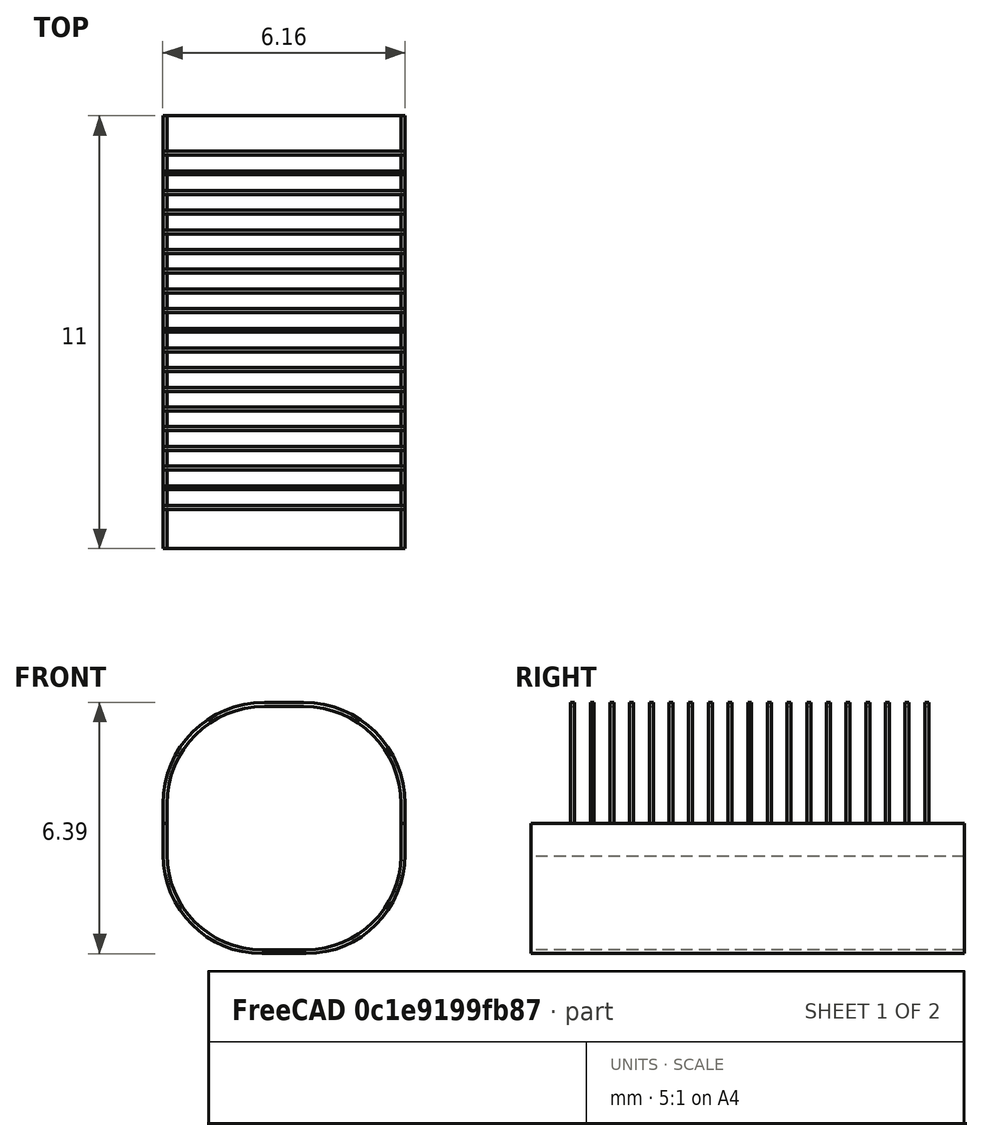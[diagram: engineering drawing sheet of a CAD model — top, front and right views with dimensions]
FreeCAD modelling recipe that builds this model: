
FCSTD DOCUMENT  (FreeCAD 0.16R6712 (Git))
Label: anode
License: All rights reserved
LicenseURL: http://en.wikipedia.org/wiki/All_rights_reserved
objects: Sketcher::SketchObject×39, Part::Sweep×19, Part::MultiFuse×1, PartDesign::Pad×1, Mesh::Feature×1
note: 61 computed .brp shape members not serialized (recipe doc carries the construction recipe); baked Part::Feature solids carry a one-line shape summary decoded from their .brp

FEATURE [Sketcher::SketchObject] Sketch
  Placement = pos=(0,0,0) rot=(1,0,0;1.5708rad)
  sketch-geometry (5):
    g0: LineSegment StartX=-0.5 StartY=3 StartZ=0 EndX=0.5 EndY=3 EndZ=0
    g1: LineSegment StartX=3 StartY=0.5 StartZ=0 EndX=3 EndY=0 EndZ=0
    g2: LineSegment StartX=-3 StartY=0 StartZ=0 EndX=-3 EndY=0.5 EndZ=0
    g3: ArcOfCircle CenterX=-0.5 CenterY=0.5 CenterZ=0 NormalX=0 NormalY=0 NormalZ=1 Radius=2.5 StartAngle=1.5708 EndAngle=3.14159
    g4: ArcOfCircle CenterX=0.5 CenterY=0.5 CenterZ=0 NormalX=0 NormalY=0 NormalZ=1 Radius=2.5 StartAngle=0 EndAngle=1.5708
  constraints (12):
    c: Horizontal(g0)
    c: Vertical(g1)
    c: Tangent(g0,g3) = 1.5708
    c: Tangent(g2,g3) = 1.5708
    c: Tangent(g1,g4) = 1.5708
    c: Tangent(g0,g4) = 1.5708
    c: Equal(g4,g3)
    c: Radius(g4) = 2.5
    c: DistanceY(g-1,g0) = 3
    c: Symmetric(g1,g2,g-2)
    c: DistanceX(g2,g-1) = 3
    c: PointOnObject(g1,g-1)
FEATURE [Sketcher::SketchObject] Sketch001
  sketch-geometry (4):
    g0: LineSegment StartX=2.975 StartY=-0.05 StartZ=0 EndX=3.075 EndY=-0.05 EndZ=0
    g1: LineSegment StartX=3.075 StartY=-0.05 StartZ=0 EndX=3.075 EndY=0.05 EndZ=0
    g2: LineSegment StartX=3.075 StartY=0.05 StartZ=0 EndX=2.975 EndY=0.05 EndZ=0
    g3: LineSegment StartX=2.975 StartY=0.05 StartZ=0 EndX=2.975 EndY=-0.05 EndZ=0
  constraints (12):
    c: Coincident(g0,g1)
    c: Coincident(g1,g2)
    c: Coincident(g2,g3)
    c: Coincident(g3,g0)
    c: Horizontal(g0)
    c: Horizontal(g2)
    c: Vertical(g1)
    c: Vertical(g3)
    c: Distance(g1,g3) = 0.1
    c: DistanceX(g-2,g0) = 2.975
    c: Symmetric(g0,g1,g-1)
    c: DistanceY(g0,g1) = 0.1
FEATURE [Part::Sweep] Sweep
  Frenet = false
  Sections = -> [Sketch001]
  Solid = true
  Spine = -> Sketch [Edge4,Edge3,Edge2,Edge1,Edge5]
  Transition = 1
FEATURE [Sketcher::SketchObject] Sketch002
  Placement = pos=(0,0,0) rot=(1,0,0;1.5708rad)
  sketch-geometry (5):
    g0: LineSegment StartX=-0.5 StartY=3 StartZ=0 EndX=0.5 EndY=3 EndZ=0
    g1: LineSegment StartX=3 StartY=0.5 StartZ=0 EndX=3 EndY=0 EndZ=0
    g2: LineSegment StartX=-3 StartY=0 StartZ=0 EndX=-3 EndY=0.5 EndZ=0
    g3: ArcOfCircle CenterX=-0.5 CenterY=0.5 CenterZ=0 NormalX=0 NormalY=0 NormalZ=1 Radius=2.5 StartAngle=1.5708 EndAngle=3.14159
    g4: ArcOfCircle CenterX=0.5 CenterY=0.5 CenterZ=0 NormalX=0 NormalY=0 NormalZ=1 Radius=2.5 StartAngle=0 EndAngle=1.5708
  constraints (12):
    c: Horizontal(g0)
    c: Vertical(g1)
    c: Tangent(g0,g3) = 1.5708
    c: Tangent(g2,g3) = 1.5708
    c: Tangent(g1,g4) = 1.5708
    c: Tangent(g0,g4) = 1.5708
    c: Equal(g4,g3)
    c: Radius(g4) = 2.5
    c: DistanceY(g-1,g0) = 3
    c: Symmetric(g1,g2,g-2)
    c: DistanceX(g2,g-1) = 3
    c: PointOnObject(g1,g-1)
FEATURE [Sketcher::SketchObject] Sketch003
  sketch-geometry (4):
    g0: LineSegment StartX=2.975 StartY=-0.05 StartZ=0 EndX=3.075 EndY=-0.05 EndZ=0
    g1: LineSegment StartX=3.075 StartY=-0.05 StartZ=0 EndX=3.075 EndY=0.05 EndZ=0
    g2: LineSegment StartX=3.075 StartY=0.05 StartZ=0 EndX=2.975 EndY=0.05 EndZ=0
    g3: LineSegment StartX=2.975 StartY=0.05 StartZ=0 EndX=2.975 EndY=-0.05 EndZ=0
  constraints (12):
    c: Coincident(g0,g1)
    c: Coincident(g1,g2)
    c: Coincident(g2,g3)
    c: Coincident(g3,g0)
    c: Horizontal(g0)
    c: Horizontal(g2)
    c: Vertical(g1)
    c: Vertical(g3)
    c: Distance(g1,g3) = 0.1
    c: DistanceX(g-2,g0) = 2.975
    c: Symmetric(g0,g1,g-1)
    c: DistanceY(g0,g1) = 0.1
FEATURE [Part::Sweep] Sweep001
  Frenet = false
  Placement = pos=(0,0.5,0) rot=(0,0,1;0rad)
  Sections = -> [Sketch003]
  Solid = true
  Spine = -> Sketch002 [Edge4,Edge3,Edge2,Edge1,Edge5]
  Transition = 1
FEATURE [Sketcher::SketchObject] Sketch004
  Placement = pos=(0,0,0) rot=(1,0,0;1.5708rad)
  sketch-geometry (5):
    g0: LineSegment StartX=-0.5 StartY=3 StartZ=0 EndX=0.5 EndY=3 EndZ=0
    g1: LineSegment StartX=3 StartY=0.5 StartZ=0 EndX=3 EndY=0 EndZ=0
    g2: LineSegment StartX=-3 StartY=0 StartZ=0 EndX=-3 EndY=0.5 EndZ=0
    g3: ArcOfCircle CenterX=-0.5 CenterY=0.5 CenterZ=0 NormalX=0 NormalY=0 NormalZ=1 Radius=2.5 StartAngle=1.5708 EndAngle=3.14159
    g4: ArcOfCircle CenterX=0.5 CenterY=0.5 CenterZ=0 NormalX=0 NormalY=0 NormalZ=1 Radius=2.5 StartAngle=0 EndAngle=1.5708
  constraints (12):
    c: Horizontal(g0)
    c: Vertical(g1)
    c: Tangent(g0,g3) = 1.5708
    c: Tangent(g2,g3) = 1.5708
    c: Tangent(g1,g4) = 1.5708
    c: Tangent(g0,g4) = 1.5708
    c: Equal(g4,g3)
    c: Radius(g4) = 2.5
    c: DistanceY(g-1,g0) = 3
    c: Symmetric(g1,g2,g-2)
    c: DistanceX(g2,g-1) = 3
    c: PointOnObject(g1,g-1)
FEATURE [Sketcher::SketchObject] Sketch005
  sketch-geometry (4):
    g0: LineSegment StartX=2.975 StartY=-0.05 StartZ=0 EndX=3.075 EndY=-0.05 EndZ=0
    g1: LineSegment StartX=3.075 StartY=-0.05 StartZ=0 EndX=3.075 EndY=0.05 EndZ=0
    g2: LineSegment StartX=3.075 StartY=0.05 StartZ=0 EndX=2.975 EndY=0.05 EndZ=0
    g3: LineSegment StartX=2.975 StartY=0.05 StartZ=0 EndX=2.975 EndY=-0.05 EndZ=0
  constraints (12):
    c: Coincident(g0,g1)
    c: Coincident(g1,g2)
    c: Coincident(g2,g3)
    c: Coincident(g3,g0)
    c: Horizontal(g0)
    c: Horizontal(g2)
    c: Vertical(g1)
    c: Vertical(g3)
    c: Distance(g1,g3) = 0.1
    c: DistanceX(g-2,g0) = 2.975
    c: Symmetric(g0,g1,g-1)
    c: DistanceY(g0,g1) = 0.1
FEATURE [Part::Sweep] Sweep002
  Frenet = false
  Placement = pos=(0,1,0) rot=(0,0,1;0rad)
  Sections = -> [Sketch005]
  Solid = true
  Spine = -> Sketch004 [Edge4,Edge3,Edge2,Edge1,Edge5]
  Transition = 1
FEATURE [Sketcher::SketchObject] Sketch006
  Placement = pos=(0,0,0) rot=(1,0,0;1.5708rad)
  sketch-geometry (5):
    g0: LineSegment StartX=-0.5 StartY=3 StartZ=0 EndX=0.5 EndY=3 EndZ=0
    g1: LineSegment StartX=3 StartY=0.5 StartZ=0 EndX=3 EndY=0 EndZ=0
    g2: LineSegment StartX=-3 StartY=0 StartZ=0 EndX=-3 EndY=0.5 EndZ=0
    g3: ArcOfCircle CenterX=-0.5 CenterY=0.5 CenterZ=0 NormalX=0 NormalY=0 NormalZ=1 Radius=2.5 StartAngle=1.5708 EndAngle=3.14159
    g4: ArcOfCircle CenterX=0.5 CenterY=0.5 CenterZ=0 NormalX=0 NormalY=0 NormalZ=1 Radius=2.5 StartAngle=0 EndAngle=1.5708
  constraints (12):
    c: Horizontal(g0)
    c: Vertical(g1)
    c: Tangent(g0,g3) = 1.5708
    c: Tangent(g2,g3) = 1.5708
    c: Tangent(g1,g4) = 1.5708
    c: Tangent(g0,g4) = 1.5708
    c: Equal(g4,g3)
    c: Radius(g4) = 2.5
    c: DistanceY(g-1,g0) = 3
    c: Symmetric(g1,g2,g-2)
    c: DistanceX(g2,g-1) = 3
    c: PointOnObject(g1,g-1)
FEATURE [Sketcher::SketchObject] Sketch007
  sketch-geometry (4):
    g0: LineSegment StartX=2.975 StartY=-0.05 StartZ=0 EndX=3.075 EndY=-0.05 EndZ=0
    g1: LineSegment StartX=3.075 StartY=-0.05 StartZ=0 EndX=3.075 EndY=0.05 EndZ=0
    g2: LineSegment StartX=3.075 StartY=0.05 StartZ=0 EndX=2.975 EndY=0.05 EndZ=0
    g3: LineSegment StartX=2.975 StartY=0.05 StartZ=0 EndX=2.975 EndY=-0.05 EndZ=0
  constraints (12):
    c: Coincident(g0,g1)
    c: Coincident(g1,g2)
    c: Coincident(g2,g3)
    c: Coincident(g3,g0)
    c: Horizontal(g0)
    c: Horizontal(g2)
    c: Vertical(g1)
    c: Vertical(g3)
    c: Distance(g1,g3) = 0.1
    c: DistanceX(g-2,g0) = 2.975
    c: Symmetric(g0,g1,g-1)
    c: DistanceY(g0,g1) = 0.1
FEATURE [Part::Sweep] Sweep003
  Frenet = false
  Placement = pos=(0,1.5,0) rot=(0,0,1;0rad)
  Sections = -> [Sketch007]
  Solid = true
  Spine = -> Sketch006 [Edge4,Edge3,Edge2,Edge1,Edge5]
  Transition = 1
FEATURE [Sketcher::SketchObject] Sketch008
  Placement = pos=(0,2,0) rot=(1,0,0;1.5708rad)
  sketch-geometry (5):
    g0: LineSegment StartX=-0.5 StartY=3 StartZ=0 EndX=0.5 EndY=3 EndZ=0
    g1: LineSegment StartX=3 StartY=0.5 StartZ=0 EndX=3 EndY=0 EndZ=0
    g2: LineSegment StartX=-3 StartY=0 StartZ=0 EndX=-3 EndY=0.5 EndZ=0
    g3: ArcOfCircle CenterX=-0.5 CenterY=0.5 CenterZ=0 NormalX=0 NormalY=0 NormalZ=1 Radius=2.5 StartAngle=1.5708 EndAngle=3.14159
    g4: ArcOfCircle CenterX=0.5 CenterY=0.5 CenterZ=0 NormalX=0 NormalY=0 NormalZ=1 Radius=2.5 StartAngle=0 EndAngle=1.5708
  constraints (12):
    c: Horizontal(g0)
    c: Vertical(g1)
    c: Tangent(g0,g3) = 1.5708
    c: Tangent(g2,g3) = 1.5708
    c: Tangent(g1,g4) = 1.5708
    c: Tangent(g0,g4) = 1.5708
    c: Equal(g4,g3)
    c: Radius(g4) = 2.5
    c: DistanceY(g-1,g0) = 3
    c: Symmetric(g1,g2,g-2)
    c: DistanceX(g2,g-1) = 3
    c: PointOnObject(g1,g-1)
FEATURE [Sketcher::SketchObject] Sketch009
  sketch-geometry (4):
    g0: LineSegment StartX=2.975 StartY=-0.05 StartZ=0 EndX=3.075 EndY=-0.05 EndZ=0
    g1: LineSegment StartX=3.075 StartY=-0.05 StartZ=0 EndX=3.075 EndY=0.05 EndZ=0
    g2: LineSegment StartX=3.075 StartY=0.05 StartZ=0 EndX=2.975 EndY=0.05 EndZ=0
    g3: LineSegment StartX=2.975 StartY=0.05 StartZ=0 EndX=2.975 EndY=-0.05 EndZ=0
  constraints (12):
    c: Coincident(g0,g1)
    c: Coincident(g1,g2)
    c: Coincident(g2,g3)
    c: Coincident(g3,g0)
    c: Horizontal(g0)
    c: Horizontal(g2)
    c: Vertical(g1)
    c: Vertical(g3)
    c: Distance(g1,g3) = 0.1
    c: DistanceX(g-2,g0) = 2.975
    c: Symmetric(g0,g1,g-1)
    c: DistanceY(g0,g1) = 0.1
FEATURE [Part::Sweep] Sweep004
  Frenet = false
  Placement = pos=(0,2,0) rot=(0,0,1;0rad)
  Sections = -> [Sketch009]
  Solid = true
  Spine = -> Sketch008 [Edge4,Edge3,Edge2,Edge1,Edge5]
  Transition = 1
FEATURE [Sketcher::SketchObject] Sketch010
  Placement = pos=(0,0,0) rot=(1,0,0;1.5708rad)
  sketch-geometry (5):
    g0: LineSegment StartX=-0.5 StartY=3 StartZ=0 EndX=0.5 EndY=3 EndZ=0
    g1: LineSegment StartX=3 StartY=0.5 StartZ=0 EndX=3 EndY=0 EndZ=0
    g2: LineSegment StartX=-3 StartY=0 StartZ=0 EndX=-3 EndY=0.5 EndZ=0
    g3: ArcOfCircle CenterX=-0.5 CenterY=0.5 CenterZ=0 NormalX=0 NormalY=0 NormalZ=1 Radius=2.5 StartAngle=1.5708 EndAngle=3.14159
    g4: ArcOfCircle CenterX=0.5 CenterY=0.5 CenterZ=0 NormalX=0 NormalY=0 NormalZ=1 Radius=2.5 StartAngle=0 EndAngle=1.5708
  constraints (12):
    c: Horizontal(g0)
    c: Vertical(g1)
    c: Tangent(g0,g3) = 1.5708
    c: Tangent(g2,g3) = 1.5708
    c: Tangent(g1,g4) = 1.5708
    c: Tangent(g0,g4) = 1.5708
    c: Equal(g4,g3)
    c: Radius(g4) = 2.5
    c: DistanceY(g-1,g0) = 3
    c: Symmetric(g1,g2,g-2)
    c: DistanceX(g2,g-1) = 3
    c: PointOnObject(g1,g-1)
FEATURE [Sketcher::SketchObject] Sketch011
  sketch-geometry (4):
    g0: LineSegment StartX=2.975 StartY=-0.05 StartZ=0 EndX=3.075 EndY=-0.05 EndZ=0
    g1: LineSegment StartX=3.075 StartY=-0.05 StartZ=0 EndX=3.075 EndY=0.05 EndZ=0
    g2: LineSegment StartX=3.075 StartY=0.05 StartZ=0 EndX=2.975 EndY=0.05 EndZ=0
    g3: LineSegment StartX=2.975 StartY=0.05 StartZ=0 EndX=2.975 EndY=-0.05 EndZ=0
  constraints (12):
    c: Coincident(g0,g1)
    c: Coincident(g1,g2)
    c: Coincident(g2,g3)
    c: Coincident(g3,g0)
    c: Horizontal(g0)
    c: Horizontal(g2)
    c: Vertical(g1)
    c: Vertical(g3)
    c: Distance(g1,g3) = 0.1
    c: DistanceX(g-2,g0) = 2.975
    c: Symmetric(g0,g1,g-1)
    c: DistanceY(g0,g1) = 0.1
FEATURE [Part::Sweep] Sweep005
  Frenet = false
  Placement = pos=(0,2.5,0) rot=(0,0,1;0rad)
  Sections = -> [Sketch011]
  Solid = true
  Spine = -> Sketch010 [Edge4,Edge3,Edge2,Edge1,Edge5]
  Transition = 1
FEATURE [Sketcher::SketchObject] Sketch012
  Placement = pos=(0,0,0) rot=(1,0,0;1.5708rad)
  sketch-geometry (5):
    g0: LineSegment StartX=-0.5 StartY=3 StartZ=0 EndX=0.5 EndY=3 EndZ=0
    g1: LineSegment StartX=3 StartY=0.5 StartZ=0 EndX=3 EndY=0 EndZ=0
    g2: LineSegment StartX=-3 StartY=0 StartZ=0 EndX=-3 EndY=0.5 EndZ=0
    g3: ArcOfCircle CenterX=-0.5 CenterY=0.5 CenterZ=0 NormalX=0 NormalY=0 NormalZ=1 Radius=2.5 StartAngle=1.5708 EndAngle=3.14159
    g4: ArcOfCircle CenterX=0.5 CenterY=0.5 CenterZ=0 NormalX=0 NormalY=0 NormalZ=1 Radius=2.5 StartAngle=0 EndAngle=1.5708
  constraints (12):
    c: Horizontal(g0)
    c: Vertical(g1)
    c: Tangent(g0,g3) = 1.5708
    c: Tangent(g2,g3) = 1.5708
    c: Tangent(g1,g4) = 1.5708
    c: Tangent(g0,g4) = 1.5708
    c: Equal(g4,g3)
    c: Radius(g4) = 2.5
    c: DistanceY(g-1,g0) = 3
    c: Symmetric(g1,g2,g-2)
    c: DistanceX(g2,g-1) = 3
    c: PointOnObject(g1,g-1)
FEATURE [Sketcher::SketchObject] Sketch013
  sketch-geometry (4):
    g0: LineSegment StartX=2.975 StartY=-0.05 StartZ=0 EndX=3.075 EndY=-0.05 EndZ=0
    g1: LineSegment StartX=3.075 StartY=-0.05 StartZ=0 EndX=3.075 EndY=0.05 EndZ=0
    g2: LineSegment StartX=3.075 StartY=0.05 StartZ=0 EndX=2.975 EndY=0.05 EndZ=0
    g3: LineSegment StartX=2.975 StartY=0.05 StartZ=0 EndX=2.975 EndY=-0.05 EndZ=0
  constraints (12):
    c: Coincident(g0,g1)
    c: Coincident(g1,g2)
    c: Coincident(g2,g3)
    c: Coincident(g3,g0)
    c: Horizontal(g0)
    c: Horizontal(g2)
    c: Vertical(g1)
    c: Vertical(g3)
    c: Distance(g1,g3) = 0.1
    c: DistanceX(g-2,g0) = 2.975
    c: Symmetric(g0,g1,g-1)
    c: DistanceY(g0,g1) = 0.1
FEATURE [Part::Sweep] Sweep006
  Frenet = false
  Placement = pos=(0,3,0) rot=(0,0,1;0rad)
  Sections = -> [Sketch013]
  Solid = true
  Spine = -> Sketch012 [Edge4,Edge3,Edge2,Edge1,Edge5]
  Transition = 1
FEATURE [Sketcher::SketchObject] Sketch014
  Placement = pos=(0,0,0) rot=(1,0,0;1.5708rad)
  sketch-geometry (5):
    g0: LineSegment StartX=-0.5 StartY=3 StartZ=0 EndX=0.5 EndY=3 EndZ=0
    g1: LineSegment StartX=3 StartY=0.5 StartZ=0 EndX=3 EndY=0 EndZ=0
    g2: LineSegment StartX=-3 StartY=0 StartZ=0 EndX=-3 EndY=0.5 EndZ=0
    g3: ArcOfCircle CenterX=-0.5 CenterY=0.5 CenterZ=0 NormalX=0 NormalY=0 NormalZ=1 Radius=2.5 StartAngle=1.5708 EndAngle=3.14159
    g4: ArcOfCircle CenterX=0.5 CenterY=0.5 CenterZ=0 NormalX=0 NormalY=0 NormalZ=1 Radius=2.5 StartAngle=0 EndAngle=1.5708
  constraints (12):
    c: Horizontal(g0)
    c: Vertical(g1)
    c: Tangent(g0,g3) = 1.5708
    c: Tangent(g2,g3) = 1.5708
    c: Tangent(g1,g4) = 1.5708
    c: Tangent(g0,g4) = 1.5708
    c: Equal(g4,g3)
    c: Radius(g4) = 2.5
    c: DistanceY(g-1,g0) = 3
    c: Symmetric(g1,g2,g-2)
    c: DistanceX(g2,g-1) = 3
    c: PointOnObject(g1,g-1)
FEATURE [Sketcher::SketchObject] Sketch015
  sketch-geometry (4):
    g0: LineSegment StartX=2.975 StartY=-0.05 StartZ=0 EndX=3.075 EndY=-0.05 EndZ=0
    g1: LineSegment StartX=3.075 StartY=-0.05 StartZ=0 EndX=3.075 EndY=0.05 EndZ=0
    g2: LineSegment StartX=3.075 StartY=0.05 StartZ=0 EndX=2.975 EndY=0.05 EndZ=0
    g3: LineSegment StartX=2.975 StartY=0.05 StartZ=0 EndX=2.975 EndY=-0.05 EndZ=0
  constraints (12):
    c: Coincident(g0,g1)
    c: Coincident(g1,g2)
    c: Coincident(g2,g3)
    c: Coincident(g3,g0)
    c: Horizontal(g0)
    c: Horizontal(g2)
    c: Vertical(g1)
    c: Vertical(g3)
    c: Distance(g1,g3) = 0.1
    c: DistanceX(g-2,g0) = 2.975
    c: Symmetric(g0,g1,g-1)
    c: DistanceY(g0,g1) = 0.1
FEATURE [Part::Sweep] Sweep007
  Frenet = false
  Placement = pos=(0,3.5,0) rot=(0,0,1;0rad)
  Sections = -> [Sketch015]
  Solid = true
  Spine = -> Sketch014 [Edge4,Edge3,Edge2,Edge1,Edge5]
  Transition = 1
FEATURE [Sketcher::SketchObject] Sketch016
  Placement = pos=(0,0,0) rot=(1,0,0;1.5708rad)
  sketch-geometry (5):
    g0: LineSegment StartX=-0.5 StartY=3 StartZ=0 EndX=0.5 EndY=3 EndZ=0
    g1: LineSegment StartX=3 StartY=0.5 StartZ=0 EndX=3 EndY=0 EndZ=0
    g2: LineSegment StartX=-3 StartY=0 StartZ=0 EndX=-3 EndY=0.5 EndZ=0
    g3: ArcOfCircle CenterX=-0.5 CenterY=0.5 CenterZ=0 NormalX=0 NormalY=0 NormalZ=1 Radius=2.5 StartAngle=1.5708 EndAngle=3.14159
    g4: ArcOfCircle CenterX=0.5 CenterY=0.5 CenterZ=0 NormalX=0 NormalY=0 NormalZ=1 Radius=2.5 StartAngle=0 EndAngle=1.5708
  constraints (12):
    c: Horizontal(g0)
    c: Vertical(g1)
    c: Tangent(g0,g3) = 1.5708
    c: Tangent(g2,g3) = 1.5708
    c: Tangent(g1,g4) = 1.5708
    c: Tangent(g0,g4) = 1.5708
    c: Equal(g4,g3)
    c: Radius(g4) = 2.5
    c: DistanceY(g-1,g0) = 3
    c: Symmetric(g1,g2,g-2)
    c: DistanceX(g2,g-1) = 3
    c: PointOnObject(g1,g-1)
FEATURE [Sketcher::SketchObject] Sketch017
  sketch-geometry (4):
    g0: LineSegment StartX=2.975 StartY=-0.05 StartZ=0 EndX=3.075 EndY=-0.05 EndZ=0
    g1: LineSegment StartX=3.075 StartY=-0.05 StartZ=0 EndX=3.075 EndY=0.05 EndZ=0
    g2: LineSegment StartX=3.075 StartY=0.05 StartZ=0 EndX=2.975 EndY=0.05 EndZ=0
    g3: LineSegment StartX=2.975 StartY=0.05 StartZ=0 EndX=2.975 EndY=-0.05 EndZ=0
  constraints (12):
    c: Coincident(g0,g1)
    c: Coincident(g1,g2)
    c: Coincident(g2,g3)
    c: Coincident(g3,g0)
    c: Horizontal(g0)
    c: Horizontal(g2)
    c: Vertical(g1)
    c: Vertical(g3)
    c: Distance(g1,g3) = 0.1
    c: DistanceX(g-2,g0) = 2.975
    c: Symmetric(g0,g1,g-1)
    c: DistanceY(g0,g1) = 0.1
FEATURE [Part::Sweep] Sweep008
  Frenet = false
  Placement = pos=(0,4,0) rot=(0,0,1;0rad)
  Sections = -> [Sketch017]
  Solid = true
  Spine = -> Sketch016 [Edge4,Edge3,Edge2,Edge1,Edge5]
  Transition = 1
FEATURE [Sketcher::SketchObject] Sketch018
  Placement = pos=(0,0,0) rot=(1,0,0;1.5708rad)
  sketch-geometry (5):
    g0: LineSegment StartX=-0.5 StartY=3 StartZ=0 EndX=0.5 EndY=3 EndZ=0
    g1: LineSegment StartX=3 StartY=0.5 StartZ=0 EndX=3 EndY=0 EndZ=0
    g2: LineSegment StartX=-3 StartY=0 StartZ=0 EndX=-3 EndY=0.5 EndZ=0
    g3: ArcOfCircle CenterX=-0.5 CenterY=0.5 CenterZ=0 NormalX=0 NormalY=0 NormalZ=1 Radius=2.5 StartAngle=1.5708 EndAngle=3.14159
    g4: ArcOfCircle CenterX=0.5 CenterY=0.5 CenterZ=0 NormalX=0 NormalY=0 NormalZ=1 Radius=2.5 StartAngle=0 EndAngle=1.5708
  constraints (12):
    c: Horizontal(g0)
    c: Vertical(g1)
    c: Tangent(g0,g3) = 1.5708
    c: Tangent(g2,g3) = 1.5708
    c: Tangent(g1,g4) = 1.5708
    c: Tangent(g0,g4) = 1.5708
    c: Equal(g4,g3)
    c: Radius(g4) = 2.5
    c: DistanceY(g-1,g0) = 3
    c: Symmetric(g1,g2,g-2)
    c: DistanceX(g2,g-1) = 3
    c: PointOnObject(g1,g-1)
FEATURE [Sketcher::SketchObject] Sketch019
  sketch-geometry (4):
    g0: LineSegment StartX=2.975 StartY=-0.05 StartZ=0 EndX=3.075 EndY=-0.05 EndZ=0
    g1: LineSegment StartX=3.075 StartY=-0.05 StartZ=0 EndX=3.075 EndY=0.05 EndZ=0
    g2: LineSegment StartX=3.075 StartY=0.05 StartZ=0 EndX=2.975 EndY=0.05 EndZ=0
    g3: LineSegment StartX=2.975 StartY=0.05 StartZ=0 EndX=2.975 EndY=-0.05 EndZ=0
  constraints (12):
    c: Coincident(g0,g1)
    c: Coincident(g1,g2)
    c: Coincident(g2,g3)
    c: Coincident(g3,g0)
    c: Horizontal(g0)
    c: Horizontal(g2)
    c: Vertical(g1)
    c: Vertical(g3)
    c: Distance(g1,g3) = 0.1
    c: DistanceX(g-2,g0) = 2.975
    c: Symmetric(g0,g1,g-1)
    c: DistanceY(g0,g1) = 0.1
FEATURE [Part::Sweep] Sweep009
  Frenet = false
  Placement = pos=(0,4.5,0) rot=(0,0,1;0rad)
  Sections = -> [Sketch019]
  Solid = true
  Spine = -> Sketch018 [Edge4,Edge3,Edge2,Edge1,Edge5]
  Transition = 1
FEATURE [Sketcher::SketchObject] Sketch020
  Placement = pos=(0,0,0) rot=(1,0,0;1.5708rad)
  sketch-geometry (5):
    g0: LineSegment StartX=-0.5 StartY=3 StartZ=0 EndX=0.5 EndY=3 EndZ=0
    g1: LineSegment StartX=3 StartY=0.5 StartZ=0 EndX=3 EndY=0 EndZ=0
    g2: LineSegment StartX=-3 StartY=0 StartZ=0 EndX=-3 EndY=0.5 EndZ=0
    g3: ArcOfCircle CenterX=-0.5 CenterY=0.5 CenterZ=0 NormalX=0 NormalY=0 NormalZ=1 Radius=2.5 StartAngle=1.5708 EndAngle=3.14159
    g4: ArcOfCircle CenterX=0.5 CenterY=0.5 CenterZ=0 NormalX=0 NormalY=0 NormalZ=1 Radius=2.5 StartAngle=0 EndAngle=1.5708
  constraints (12):
    c: Horizontal(g0)
    c: Vertical(g1)
    c: Tangent(g0,g3) = 1.5708
    c: Tangent(g2,g3) = 1.5708
    c: Tangent(g1,g4) = 1.5708
    c: Tangent(g0,g4) = 1.5708
    c: Equal(g4,g3)
    c: Radius(g4) = 2.5
    c: DistanceY(g-1,g0) = 3
    c: Symmetric(g1,g2,g-2)
    c: DistanceX(g2,g-1) = 3
    c: PointOnObject(g1,g-1)
FEATURE [Sketcher::SketchObject] Sketch021
  sketch-geometry (4):
    g0: LineSegment StartX=2.975 StartY=-0.05 StartZ=0 EndX=3.075 EndY=-0.05 EndZ=0
    g1: LineSegment StartX=3.075 StartY=-0.05 StartZ=0 EndX=3.075 EndY=0.05 EndZ=0
    g2: LineSegment StartX=3.075 StartY=0.05 StartZ=0 EndX=2.975 EndY=0.05 EndZ=0
    g3: LineSegment StartX=2.975 StartY=0.05 StartZ=0 EndX=2.975 EndY=-0.05 EndZ=0
  constraints (12):
    c: Coincident(g0,g1)
    c: Coincident(g1,g2)
    c: Coincident(g2,g3)
    c: Coincident(g3,g0)
    c: Horizontal(g0)
    c: Horizontal(g2)
    c: Vertical(g1)
    c: Vertical(g3)
    c: Distance(g1,g3) = 0.1
    c: DistanceX(g-2,g0) = 2.975
    c: Symmetric(g0,g1,g-1)
    c: DistanceY(g0,g1) = 0.1
FEATURE [Part::Sweep] Sweep010
  Frenet = false
  Placement = pos=(0,5,0) rot=(0,0,1;0rad)
  Sections = -> [Sketch021]
  Solid = true
  Spine = -> Sketch020 [Edge4,Edge3,Edge2,Edge1,Edge5]
  Transition = 1
FEATURE [Sketcher::SketchObject] Sketch022
  Placement = pos=(0,0,0) rot=(1,0,0;1.5708rad)
  sketch-geometry (5):
    g0: LineSegment StartX=-0.5 StartY=3 StartZ=0 EndX=0.5 EndY=3 EndZ=0
    g1: LineSegment StartX=3 StartY=0.5 StartZ=0 EndX=3 EndY=0 EndZ=0
    g2: LineSegment StartX=-3 StartY=0 StartZ=0 EndX=-3 EndY=0.5 EndZ=0
    g3: ArcOfCircle CenterX=-0.5 CenterY=0.5 CenterZ=0 NormalX=0 NormalY=0 NormalZ=1 Radius=2.5 StartAngle=1.5708 EndAngle=3.14159
    g4: ArcOfCircle CenterX=0.5 CenterY=0.5 CenterZ=0 NormalX=0 NormalY=0 NormalZ=1 Radius=2.5 StartAngle=0 EndAngle=1.5708
  constraints (12):
    c: Horizontal(g0)
    c: Vertical(g1)
    c: Tangent(g0,g3) = 1.5708
    c: Tangent(g2,g3) = 1.5708
    c: Tangent(g1,g4) = 1.5708
    c: Tangent(g0,g4) = 1.5708
    c: Equal(g4,g3)
    c: Radius(g4) = 2.5
    c: DistanceY(g-1,g0) = 3
    c: Symmetric(g1,g2,g-2)
    c: DistanceX(g2,g-1) = 3
    c: PointOnObject(g1,g-1)
FEATURE [Sketcher::SketchObject] Sketch023
  sketch-geometry (4):
    g0: LineSegment StartX=2.975 StartY=-0.05 StartZ=0 EndX=3.075 EndY=-0.05 EndZ=0
    g1: LineSegment StartX=3.075 StartY=-0.05 StartZ=0 EndX=3.075 EndY=0.05 EndZ=0
    g2: LineSegment StartX=3.075 StartY=0.05 StartZ=0 EndX=2.975 EndY=0.05 EndZ=0
    g3: LineSegment StartX=2.975 StartY=0.05 StartZ=0 EndX=2.975 EndY=-0.05 EndZ=0
  constraints (12):
    c: Coincident(g0,g1)
    c: Coincident(g1,g2)
    c: Coincident(g2,g3)
    c: Coincident(g3,g0)
    c: Horizontal(g0)
    c: Horizontal(g2)
    c: Vertical(g1)
    c: Vertical(g3)
    c: Distance(g1,g3) = 0.1
    c: DistanceX(g-2,g0) = 2.975
    c: Symmetric(g0,g1,g-1)
    c: DistanceY(g0,g1) = 0.1
FEATURE [Part::Sweep] Sweep011
  Frenet = false
  Placement = pos=(0,5.5,0) rot=(0,0,1;0rad)
  Sections = -> [Sketch023]
  Solid = true
  Spine = -> Sketch022 [Edge4,Edge3,Edge2,Edge1,Edge5]
  Transition = 1
FEATURE [Sketcher::SketchObject] Sketch024
  Placement = pos=(0,0,0) rot=(1,0,0;1.5708rad)
  sketch-geometry (5):
    g0: LineSegment StartX=-0.5 StartY=3 StartZ=0 EndX=0.5 EndY=3 EndZ=0
    g1: LineSegment StartX=3 StartY=0.5 StartZ=0 EndX=3 EndY=0 EndZ=0
    g2: LineSegment StartX=-3 StartY=0 StartZ=0 EndX=-3 EndY=0.5 EndZ=0
    g3: ArcOfCircle CenterX=-0.5 CenterY=0.5 CenterZ=0 NormalX=0 NormalY=0 NormalZ=1 Radius=2.5 StartAngle=1.5708 EndAngle=3.14159
    g4: ArcOfCircle CenterX=0.5 CenterY=0.5 CenterZ=0 NormalX=0 NormalY=0 NormalZ=1 Radius=2.5 StartAngle=0 EndAngle=1.5708
  constraints (12):
    c: Horizontal(g0)
    c: Vertical(g1)
    c: Tangent(g0,g3) = 1.5708
    c: Tangent(g2,g3) = 1.5708
    c: Tangent(g1,g4) = 1.5708
    c: Tangent(g0,g4) = 1.5708
    c: Equal(g4,g3)
    c: Radius(g4) = 2.5
    c: DistanceY(g-1,g0) = 3
    c: Symmetric(g1,g2,g-2)
    c: DistanceX(g2,g-1) = 3
    c: PointOnObject(g1,g-1)
FEATURE [Sketcher::SketchObject] Sketch025
  sketch-geometry (4):
    g0: LineSegment StartX=2.975 StartY=-0.05 StartZ=0 EndX=3.075 EndY=-0.05 EndZ=0
    g1: LineSegment StartX=3.075 StartY=-0.05 StartZ=0 EndX=3.075 EndY=0.05 EndZ=0
    g2: LineSegment StartX=3.075 StartY=0.05 StartZ=0 EndX=2.975 EndY=0.05 EndZ=0
    g3: LineSegment StartX=2.975 StartY=0.05 StartZ=0 EndX=2.975 EndY=-0.05 EndZ=0
  constraints (12):
    c: Coincident(g0,g1)
    c: Coincident(g1,g2)
    c: Coincident(g2,g3)
    c: Coincident(g3,g0)
    c: Horizontal(g0)
    c: Horizontal(g2)
    c: Vertical(g1)
    c: Vertical(g3)
    c: Distance(g1,g3) = 0.1
    c: DistanceX(g-2,g0) = 2.975
    c: Symmetric(g0,g1,g-1)
    c: DistanceY(g0,g1) = 0.1
FEATURE [Part::Sweep] Sweep012
  Frenet = false
  Placement = pos=(0,6,0) rot=(0,0,1;0rad)
  Sections = -> [Sketch025]
  Solid = true
  Spine = -> Sketch024 [Edge4,Edge3,Edge2,Edge1,Edge5]
  Transition = 1
FEATURE [Sketcher::SketchObject] Sketch026
  Placement = pos=(0,0,0) rot=(1,0,0;1.5708rad)
  sketch-geometry (5):
    g0: LineSegment StartX=-0.5 StartY=3 StartZ=0 EndX=0.5 EndY=3 EndZ=0
    g1: LineSegment StartX=3 StartY=0.5 StartZ=0 EndX=3 EndY=0 EndZ=0
    g2: LineSegment StartX=-3 StartY=0 StartZ=0 EndX=-3 EndY=0.5 EndZ=0
    g3: ArcOfCircle CenterX=-0.5 CenterY=0.5 CenterZ=0 NormalX=0 NormalY=0 NormalZ=1 Radius=2.5 StartAngle=1.5708 EndAngle=3.14159
    g4: ArcOfCircle CenterX=0.5 CenterY=0.5 CenterZ=0 NormalX=0 NormalY=0 NormalZ=1 Radius=2.5 StartAngle=0 EndAngle=1.5708
  constraints (12):
    c: Horizontal(g0)
    c: Vertical(g1)
    c: Tangent(g0,g3) = 1.5708
    c: Tangent(g2,g3) = 1.5708
    c: Tangent(g1,g4) = 1.5708
    c: Tangent(g0,g4) = 1.5708
    c: Equal(g4,g3)
    c: Radius(g4) = 2.5
    c: DistanceY(g-1,g0) = 3
    c: Symmetric(g1,g2,g-2)
    c: DistanceX(g2,g-1) = 3
    c: PointOnObject(g1,g-1)
FEATURE [Sketcher::SketchObject] Sketch027
  sketch-geometry (4):
    g0: LineSegment StartX=2.975 StartY=-0.05 StartZ=0 EndX=3.075 EndY=-0.05 EndZ=0
    g1: LineSegment StartX=3.075 StartY=-0.05 StartZ=0 EndX=3.075 EndY=0.05 EndZ=0
    g2: LineSegment StartX=3.075 StartY=0.05 StartZ=0 EndX=2.975 EndY=0.05 EndZ=0
    g3: LineSegment StartX=2.975 StartY=0.05 StartZ=0 EndX=2.975 EndY=-0.05 EndZ=0
  constraints (12):
    c: Coincident(g0,g1)
    c: Coincident(g1,g2)
    c: Coincident(g2,g3)
    c: Coincident(g3,g0)
    c: Horizontal(g0)
    c: Horizontal(g2)
    c: Vertical(g1)
    c: Vertical(g3)
    c: Distance(g1,g3) = 0.1
    c: DistanceX(g-2,g0) = 2.975
    c: Symmetric(g0,g1,g-1)
    c: DistanceY(g0,g1) = 0.1
FEATURE [Part::Sweep] Sweep013
  Frenet = false
  Placement = pos=(0,6.5,0) rot=(0,0,1;0rad)
  Sections = -> [Sketch027]
  Solid = true
  Spine = -> Sketch026 [Edge4,Edge3,Edge2,Edge1,Edge5]
  Transition = 1
FEATURE [Sketcher::SketchObject] Sketch028
  Placement = pos=(0,0,0) rot=(1,0,0;1.5708rad)
  sketch-geometry (5):
    g0: LineSegment StartX=-0.5 StartY=3 StartZ=0 EndX=0.5 EndY=3 EndZ=0
    g1: LineSegment StartX=3 StartY=0.5 StartZ=0 EndX=3 EndY=0 EndZ=0
    g2: LineSegment StartX=-3 StartY=0 StartZ=0 EndX=-3 EndY=0.5 EndZ=0
    g3: ArcOfCircle CenterX=-0.5 CenterY=0.5 CenterZ=0 NormalX=0 NormalY=0 NormalZ=1 Radius=2.5 StartAngle=1.5708 EndAngle=3.14159
    g4: ArcOfCircle CenterX=0.5 CenterY=0.5 CenterZ=0 NormalX=0 NormalY=0 NormalZ=1 Radius=2.5 StartAngle=0 EndAngle=1.5708
  constraints (12):
    c: Horizontal(g0)
    c: Vertical(g1)
    c: Tangent(g0,g3) = 1.5708
    c: Tangent(g2,g3) = 1.5708
    c: Tangent(g1,g4) = 1.5708
    c: Tangent(g0,g4) = 1.5708
    c: Equal(g4,g3)
    c: Radius(g4) = 2.5
    c: DistanceY(g-1,g0) = 3
    c: Symmetric(g1,g2,g-2)
    c: DistanceX(g2,g-1) = 3
    c: PointOnObject(g1,g-1)
FEATURE [Sketcher::SketchObject] Sketch029
  sketch-geometry (4):
    g0: LineSegment StartX=2.975 StartY=-0.05 StartZ=0 EndX=3.075 EndY=-0.05 EndZ=0
    g1: LineSegment StartX=3.075 StartY=-0.05 StartZ=0 EndX=3.075 EndY=0.05 EndZ=0
    g2: LineSegment StartX=3.075 StartY=0.05 StartZ=0 EndX=2.975 EndY=0.05 EndZ=0
    g3: LineSegment StartX=2.975 StartY=0.05 StartZ=0 EndX=2.975 EndY=-0.05 EndZ=0
  constraints (12):
    c: Coincident(g0,g1)
    c: Coincident(g1,g2)
    c: Coincident(g2,g3)
    c: Coincident(g3,g0)
    c: Horizontal(g0)
    c: Horizontal(g2)
    c: Vertical(g1)
    c: Vertical(g3)
    c: Distance(g1,g3) = 0.1
    c: DistanceX(g-2,g0) = 2.975
    c: Symmetric(g0,g1,g-1)
    c: DistanceY(g0,g1) = 0.1
FEATURE [Part::Sweep] Sweep014
  Frenet = false
  Placement = pos=(0,7,0) rot=(0,0,1;0rad)
  Sections = -> [Sketch029]
  Solid = true
  Spine = -> Sketch028 [Edge4,Edge3,Edge2,Edge1,Edge5]
  Transition = 1
FEATURE [Sketcher::SketchObject] Sketch030
  Placement = pos=(0,0,0) rot=(1,0,0;1.5708rad)
  sketch-geometry (5):
    g0: LineSegment StartX=-0.5 StartY=3 StartZ=0 EndX=0.5 EndY=3 EndZ=0
    g1: LineSegment StartX=3 StartY=0.5 StartZ=0 EndX=3 EndY=0 EndZ=0
    g2: LineSegment StartX=-3 StartY=0 StartZ=0 EndX=-3 EndY=0.5 EndZ=0
    g3: ArcOfCircle CenterX=-0.5 CenterY=0.5 CenterZ=0 NormalX=0 NormalY=0 NormalZ=1 Radius=2.5 StartAngle=1.5708 EndAngle=3.14159
    g4: ArcOfCircle CenterX=0.5 CenterY=0.5 CenterZ=0 NormalX=0 NormalY=0 NormalZ=1 Radius=2.5 StartAngle=0 EndAngle=1.5708
  constraints (12):
    c: Horizontal(g0)
    c: Vertical(g1)
    c: Tangent(g0,g3) = 1.5708
    c: Tangent(g2,g3) = 1.5708
    c: Tangent(g1,g4) = 1.5708
    c: Tangent(g0,g4) = 1.5708
    c: Equal(g4,g3)
    c: Radius(g4) = 2.5
    c: DistanceY(g-1,g0) = 3
    c: Symmetric(g1,g2,g-2)
    c: DistanceX(g2,g-1) = 3
    c: PointOnObject(g1,g-1)
FEATURE [Sketcher::SketchObject] Sketch031
  sketch-geometry (4):
    g0: LineSegment StartX=2.975 StartY=-0.05 StartZ=0 EndX=3.075 EndY=-0.05 EndZ=0
    g1: LineSegment StartX=3.075 StartY=-0.05 StartZ=0 EndX=3.075 EndY=0.05 EndZ=0
    g2: LineSegment StartX=3.075 StartY=0.05 StartZ=0 EndX=2.975 EndY=0.05 EndZ=0
    g3: LineSegment StartX=2.975 StartY=0.05 StartZ=0 EndX=2.975 EndY=-0.05 EndZ=0
  constraints (12):
    c: Coincident(g0,g1)
    c: Coincident(g1,g2)
    c: Coincident(g2,g3)
    c: Coincident(g3,g0)
    c: Horizontal(g0)
    c: Horizontal(g2)
    c: Vertical(g1)
    c: Vertical(g3)
    c: Distance(g1,g3) = 0.1
    c: DistanceX(g-2,g0) = 2.975
    c: Symmetric(g0,g1,g-1)
    c: DistanceY(g0,g1) = 0.1
FEATURE [Part::Sweep] Sweep015
  Frenet = false
  Placement = pos=(0,7.5,0) rot=(0,0,1;0rad)
  Sections = -> [Sketch031]
  Solid = true
  Spine = -> Sketch030 [Edge4,Edge3,Edge2,Edge1,Edge5]
  Transition = 1
FEATURE [Sketcher::SketchObject] Sketch032
  Placement = pos=(0,0,0) rot=(1,0,0;1.5708rad)
  sketch-geometry (5):
    g0: LineSegment StartX=-0.5 StartY=3 StartZ=0 EndX=0.5 EndY=3 EndZ=0
    g1: LineSegment StartX=3 StartY=0.5 StartZ=0 EndX=3 EndY=0 EndZ=0
    g2: LineSegment StartX=-3 StartY=0 StartZ=0 EndX=-3 EndY=0.5 EndZ=0
    g3: ArcOfCircle CenterX=-0.5 CenterY=0.5 CenterZ=0 NormalX=0 NormalY=0 NormalZ=1 Radius=2.5 StartAngle=1.5708 EndAngle=3.14159
    g4: ArcOfCircle CenterX=0.5 CenterY=0.5 CenterZ=0 NormalX=0 NormalY=0 NormalZ=1 Radius=2.5 StartAngle=0 EndAngle=1.5708
  constraints (12):
    c: Horizontal(g0)
    c: Vertical(g1)
    c: Tangent(g0,g3) = 1.5708
    c: Tangent(g2,g3) = 1.5708
    c: Tangent(g1,g4) = 1.5708
    c: Tangent(g0,g4) = 1.5708
    c: Equal(g4,g3)
    c: Radius(g4) = 2.5
    c: DistanceY(g-1,g0) = 3
    c: Symmetric(g1,g2,g-2)
    c: DistanceX(g2,g-1) = 3
    c: PointOnObject(g1,g-1)
FEATURE [Sketcher::SketchObject] Sketch033
  sketch-geometry (4):
    g0: LineSegment StartX=2.975 StartY=-0.05 StartZ=0 EndX=3.075 EndY=-0.05 EndZ=0
    g1: LineSegment StartX=3.075 StartY=-0.05 StartZ=0 EndX=3.075 EndY=0.05 EndZ=0
    g2: LineSegment StartX=3.075 StartY=0.05 StartZ=0 EndX=2.975 EndY=0.05 EndZ=0
    g3: LineSegment StartX=2.975 StartY=0.05 StartZ=0 EndX=2.975 EndY=-0.05 EndZ=0
  constraints (12):
    c: Coincident(g0,g1)
    c: Coincident(g1,g2)
    c: Coincident(g2,g3)
    c: Coincident(g3,g0)
    c: Horizontal(g0)
    c: Horizontal(g2)
    c: Vertical(g1)
    c: Vertical(g3)
    c: Distance(g1,g3) = 0.1
    c: DistanceX(g-2,g0) = 2.975
    c: Symmetric(g0,g1,g-1)
    c: DistanceY(g0,g1) = 0.1
FEATURE [Part::Sweep] Sweep016
  Frenet = false
  Placement = pos=(0,8,0) rot=(0,0,1;0rad)
  Sections = -> [Sketch033]
  Solid = true
  Spine = -> Sketch032 [Edge4,Edge3,Edge2,Edge1,Edge5]
  Transition = 1
FEATURE [Sketcher::SketchObject] Sketch034
  Placement = pos=(0,0,0) rot=(1,0,0;1.5708rad)
  sketch-geometry (5):
    g0: LineSegment StartX=-0.5 StartY=3 StartZ=0 EndX=0.5 EndY=3 EndZ=0
    g1: LineSegment StartX=3 StartY=0.5 StartZ=0 EndX=3 EndY=0 EndZ=0
    g2: LineSegment StartX=-3 StartY=0 StartZ=0 EndX=-3 EndY=0.5 EndZ=0
    g3: ArcOfCircle CenterX=-0.5 CenterY=0.5 CenterZ=0 NormalX=0 NormalY=0 NormalZ=1 Radius=2.5 StartAngle=1.5708 EndAngle=3.14159
    g4: ArcOfCircle CenterX=0.5 CenterY=0.5 CenterZ=0 NormalX=0 NormalY=0 NormalZ=1 Radius=2.5 StartAngle=0 EndAngle=1.5708
  constraints (12):
    c: Horizontal(g0)
    c: Vertical(g1)
    c: Tangent(g0,g3) = 1.5708
    c: Tangent(g2,g3) = 1.5708
    c: Tangent(g1,g4) = 1.5708
    c: Tangent(g0,g4) = 1.5708
    c: Equal(g4,g3)
    c: Radius(g4) = 2.5
    c: DistanceY(g-1,g0) = 3
    c: Symmetric(g1,g2,g-2)
    c: DistanceX(g2,g-1) = 3
    c: PointOnObject(g1,g-1)
FEATURE [Sketcher::SketchObject] Sketch035
  sketch-geometry (4):
    g0: LineSegment StartX=2.975 StartY=-0.05 StartZ=0 EndX=3.075 EndY=-0.05 EndZ=0
    g1: LineSegment StartX=3.075 StartY=-0.05 StartZ=0 EndX=3.075 EndY=0.05 EndZ=0
    g2: LineSegment StartX=3.075 StartY=0.05 StartZ=0 EndX=2.975 EndY=0.05 EndZ=0
    g3: LineSegment StartX=2.975 StartY=0.05 StartZ=0 EndX=2.975 EndY=-0.05 EndZ=0
  constraints (12):
    c: Coincident(g0,g1)
    c: Coincident(g1,g2)
    c: Coincident(g2,g3)
    c: Coincident(g3,g0)
    c: Horizontal(g0)
    c: Horizontal(g2)
    c: Vertical(g1)
    c: Vertical(g3)
    c: Distance(g1,g3) = 0.1
    c: DistanceX(g-2,g0) = 2.975
    c: Symmetric(g0,g1,g-1)
    c: DistanceY(g0,g1) = 0.1
FEATURE [Part::Sweep] Sweep017
  Frenet = false
  Placement = pos=(0,8.5,0) rot=(0,0,1;0rad)
  Sections = -> [Sketch035]
  Solid = true
  Spine = -> Sketch034 [Edge4,Edge3,Edge2,Edge1,Edge5]
  Transition = 1
FEATURE [Sketcher::SketchObject] Sketch036
  Placement = pos=(0,0,0) rot=(1,0,0;1.5708rad)
  sketch-geometry (5):
    g0: LineSegment StartX=-0.5 StartY=3 StartZ=0 EndX=0.5 EndY=3 EndZ=0
    g1: LineSegment StartX=3 StartY=0.5 StartZ=0 EndX=3 EndY=0 EndZ=0
    g2: LineSegment StartX=-3 StartY=0 StartZ=0 EndX=-3 EndY=0.5 EndZ=0
    g3: ArcOfCircle CenterX=-0.5 CenterY=0.5 CenterZ=0 NormalX=0 NormalY=0 NormalZ=1 Radius=2.5 StartAngle=1.5708 EndAngle=3.14159
    g4: ArcOfCircle CenterX=0.5 CenterY=0.5 CenterZ=0 NormalX=0 NormalY=0 NormalZ=1 Radius=2.5 StartAngle=0 EndAngle=1.5708
  constraints (12):
    c: Horizontal(g0)
    c: Vertical(g1)
    c: Tangent(g0,g3) = 1.5708
    c: Tangent(g2,g3) = 1.5708
    c: Tangent(g1,g4) = 1.5708
    c: Tangent(g0,g4) = 1.5708
    c: Equal(g4,g3)
    c: Radius(g4) = 2.5
    c: DistanceY(g-1,g0) = 3
    c: Symmetric(g1,g2,g-2)
    c: DistanceX(g2,g-1) = 3
    c: PointOnObject(g1,g-1)
FEATURE [Sketcher::SketchObject] Sketch037
  sketch-geometry (4):
    g0: LineSegment StartX=2.975 StartY=-0.05 StartZ=0 EndX=3.075 EndY=-0.05 EndZ=0
    g1: LineSegment StartX=3.075 StartY=-0.05 StartZ=0 EndX=3.075 EndY=0.05 EndZ=0
    g2: LineSegment StartX=3.075 StartY=0.05 StartZ=0 EndX=2.975 EndY=0.05 EndZ=0
    g3: LineSegment StartX=2.975 StartY=0.05 StartZ=0 EndX=2.975 EndY=-0.05 EndZ=0
  constraints (12):
    c: Coincident(g0,g1)
    c: Coincident(g1,g2)
    c: Coincident(g2,g3)
    c: Coincident(g3,g0)
    c: Horizontal(g0)
    c: Horizontal(g2)
    c: Vertical(g1)
    c: Vertical(g3)
    c: Distance(g1,g3) = 0.1
    c: DistanceX(g-2,g0) = 2.975
    c: Symmetric(g0,g1,g-1)
    c: DistanceY(g0,g1) = 0.1
FEATURE [Part::Sweep] Sweep018
  Frenet = false
  Placement = pos=(0,9,0) rot=(0,0,1;0rad)
  Sections = -> [Sketch037]
  Solid = true
  Spine = -> Sketch036 [Edge4,Edge3,Edge2,Edge1,Edge5]
  Transition = 1
FEATURE [Part::MultiFuse] Fusion
  Shapes = -> [Sweep,Sweep001,Sweep002,Sweep003,Sweep004,Sweep005,Sweep007,Sweep006,Sweep008,Sweep009,Sweep010,Sweep011,Sweep012,Sweep013,Sweep014,Sweep015,Sweep016,Sweep017,Sweep018]
FEATURE [Sketcher::SketchObject] Sketch038
  Placement = pos=(0,-0.05,0) rot=(1,0,0;1.5708rad)
  Support = -> Fusion [Face61]
  sketch-geometry (12):
    g0: ArcOfCircle CenterX=-0.558198 CenterY=-0.790285 CenterZ=0 NormalX=0 NormalY=0 NormalZ=1 Radius=2.51643 StartAngle=3.14159 EndAngle=4.71239
    g1: LineSegment StartX=-0.558198 StartY=-3.30671 StartZ=0 EndX=0.558198 EndY=-3.30671 EndZ=0
    g2: ArcOfCircle CenterX=-0.558198 CenterY=-0.790285 CenterZ=0 NormalX=0 NormalY=0 NormalZ=1 Radius=2.4168 StartAngle=3.14159 EndAngle=4.71239
    g3: ArcOfCircle CenterX=0.558198 CenterY=-0.789911 CenterZ=0 NormalX=0 NormalY=0 NormalZ=1 Radius=2.41717 StartAngle=4.71239 EndAngle=6.26561
    g4: LineSegment StartX=-0.558198 StartY=-3.20709 StartZ=0 EndX=0.558198 EndY=-3.20709 EndZ=0
    g5: ArcOfCircle CenterX=0.558198 CenterY=-0.789911 CenterZ=0 NormalX=0 NormalY=0 NormalZ=1 Radius=2.5168 StartAngle=4.71239 EndAngle=6.28319
    g6: LineSegment StartX=-3.07463 StartY=-0.790284 StartZ=0 EndX=-3.07463 EndY=0 EndZ=0
    g7: LineSegment StartX=-2.975 StartY=-0.790284 StartZ=0 EndX=-2.975 EndY=0 EndZ=0
    g8: LineSegment StartX=-2.975 StartY=0 StartZ=0 EndX=-3.07463 EndY=0 EndZ=0
    g9: LineSegment StartX=2.975 StartY=-0.832389 StartZ=0 EndX=2.975 EndY=0 EndZ=0
    g10: LineSegment StartX=2.975 StartY=0 StartZ=0 EndX=3.075 EndY=0 EndZ=0
    g11: LineSegment StartX=3.075 StartY=0 StartZ=0 EndX=3.075 EndY=-0.789911 EndZ=0
  constraints (35):
    c: Coincident(g1,g0)
    c: Horizontal(g1)
    c: Tangent(g1,g0)
    c: Coincident(g2,g0)
    c: Coincident(g4,g2)
    c: Horizontal(g4)
    c: Coincident(g5,g3)
    c: Coincident(g5,g1)
    c: Coincident(g6,g0)
    c: Vertical(g6)
    c: Coincident(g7,g2)
    c: Vertical(g7)
    c: Coincident(g8,g7)
    c: Coincident(g8,g6)
    c: Coincident(g9,g3)
    c: Horizontal(g8)
    c: Horizontal(g10)
    c: Vertical(g9)
    c: Vertical(g11)
    c: Coincident(g11,g5)
    c: Coincident(g11,g10)
    c: Coincident(g4,g3)
    c: Tangent(g3,g4)
    c: Tangent(g1,g5)
    c: Tangent(g2,g4)
    c: Coincident(g10,g9)
    c: Tangent(g2,g7)
    c: Tangent(g6,g0)
    c: Tangent(g5,g11)
    c: Distance(g10,g9) = 0.1
    c: PointOnObject(g9,g-1)
    c: PointOnObject(g7,g-1)
    c: Symmetric(g2,g3,g-2)
    c: DistanceX(g-2,g9) = 2.975
    c: DistanceX(g-2,g7) = -2.975
FEATURE [PartDesign::Pad] Pad
  Length = 1
  Length2 = 10
  Reversed = true
  Sketch = -> Sketch038
  Type = 4
FEATURE [Mesh::Feature] Mesh  label="Pad (Meshed)"
